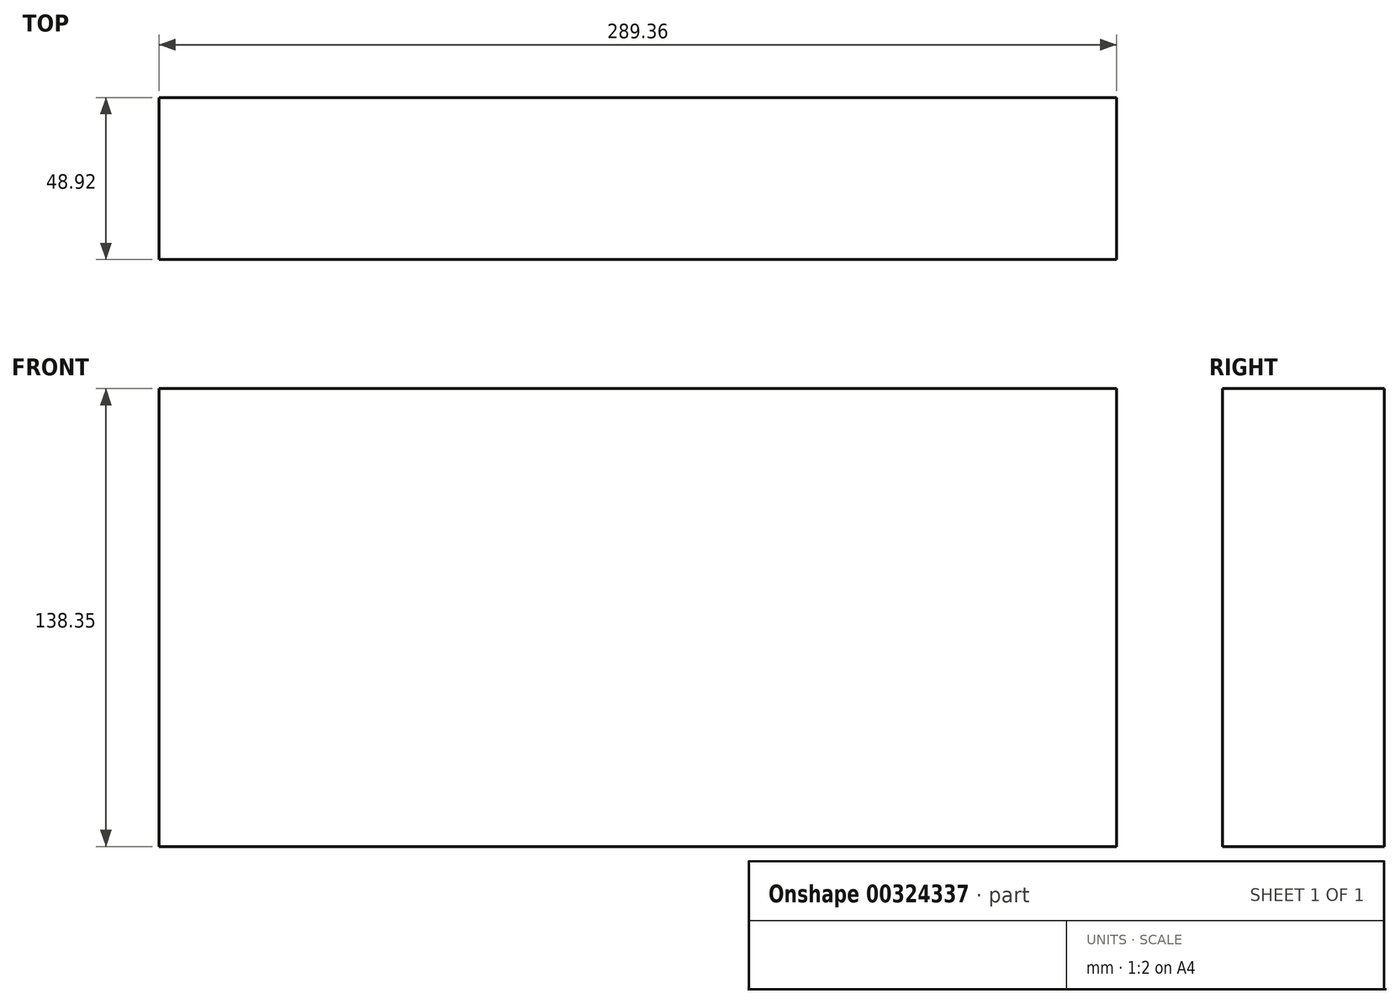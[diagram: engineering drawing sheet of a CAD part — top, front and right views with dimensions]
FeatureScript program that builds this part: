
annotation { "Feature Type Name" : "Feature", "Feature Type Description" : "" }
export const myFeature = defineFeature(function(context is Context, id is Id, definition is map)
    precondition{}
    {
        {
            var Q0;
            Q0=qCreatedBy(makeId("Front.planeOp"),FACE);
            var sketch = newSketch(context, id + "F0", { "sketchPlane" : qUnion([Q0])});
            skLineSegment(sketch, "E0.bottom", {"start": v(24.19, -48.98) * mm, "end": v(-24.19, -48.98) * mm});
            skLineSegment(sketch, "E0.top", {"start": v(24.19, 48.98) * mm, "end": v(-24.19, 48.98) * mm});
            skLineSegment(sketch, "E0.left", {"start": v(24.19, -48.98) * mm, "end": v(24.19, 48.98) * mm});
            skLineSegment(sketch, "E0.right", {"start": v(-24.19, -48.98) * mm, "end": v(-24.19, 48.98) * mm});
            skPoint(sketch, "E0.middle", {"position": v(0, 0) * mm});
            skSolve(sketch);
        }
        {
            var Q0;
            Q0=makeQuery(id+"F0.imprint","IMPRINT",FACE,{"disambiguationData":[TD([[makeQuery(id+"F0.imprint","IMPRINT",EDGE,{"derivedFrom":sQuery(id+"F0.wireOp",EDGE,"E0.bottom")}),-1.0]])]});
            var Q1;
            Q1 = qBodyType(qCreatedBy(id + "F0" ,EDGE), BodyType.WIRE);
            extrude(context, id + "F1", {"entities" : qUnion([Q0]), "surfaceEntities" : qUnion([Q1]), "endBound" : BoundingType.SYMMETRIC, "depth" : 48.9 * mm});
        }
        {
            var Q0;
            Q0=makeQuery(id+"F1.opExtrude","SWEPT_FACE",FACE,{"disambiguationData":[OSD([sQuery(id+"F0.wireOp",EDGE,"E0.top")])]});
            extrude(context, id + "F2", {"entities" : qUnion([Q0]), "operationType" : NewBodyOperationType.ADD, "endBound" : BoundingType.SYMMETRIC, "depth" : 80.76 * mm});
        }
        {
            var Q0;
            {var subQ0=sQuery(id+"F0.wireOp",EDGE,"E0.left");Q0=makeQuery(id+"F2.boolean.opBoolean","MERGE",FACE,{"derivedFrom":[makeQuery(id+"F1.opExtrude","SWEPT_FACE",FACE,{"disambiguationData":[OSD([subQ0])]}),makeQuery(id+"F2.opExtrude","SWEPT_FACE",FACE,{"disambiguationData":[OSD([sQuery(id+"F0.wireOp",EDGE,"E0.top"),subQ0])]})]});}
            extrude(context, id + "F3", {"entities" : qUnion([Q0]), "operationType" : NewBodyOperationType.ADD, "depth" : 51.9 * mm});
        }
        {
            var Q0;
            Q0=makeQuery(id+"F3.opExtrude","CAP_FACE",FACE,{"disambiguationData":[OSD([sQuery(id+"F0.wireOp",EDGE,"E0.top"),sQuery(id+"F0.wireOp",EDGE,"E0.left")])],"isStart":false});
            extrude(context, id + "F4", {"entities" : qUnion([Q0]), "operationType" : NewBodyOperationType.ADD, "endBound" : BoundingType.SYMMETRIC, "depth" : 289.36 * mm});
        }
    });
